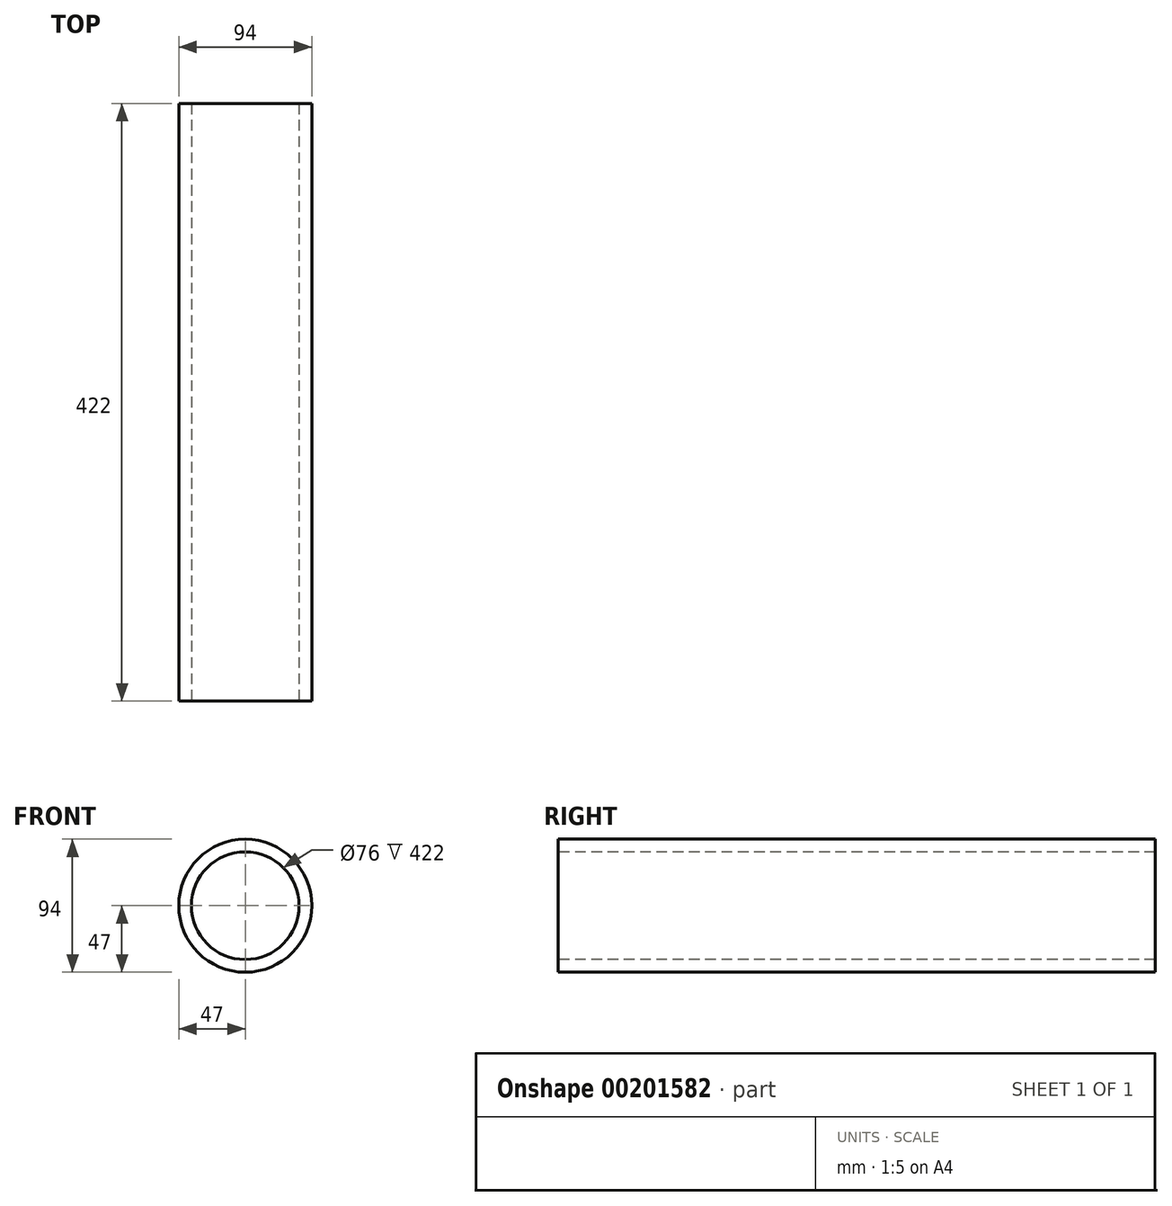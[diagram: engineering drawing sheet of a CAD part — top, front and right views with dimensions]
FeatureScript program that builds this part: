
annotation { "Feature Type Name" : "Feature", "Feature Type Description" : "" }
export const myFeature = defineFeature(function(context is Context, id is Id, definition is map)
    precondition{}
    {
        {
            var Q0;
            Q0=qCreatedBy(makeId("Front.planeOp"),FACE);
            var sketch = newSketch(context, id + "F0", { "sketchPlane" : qUnion([Q0])});
            skCircle(sketch, "E0", {"center": v(0, 0) * mm, "radius": 38 * mm});
            skCircle(sketch, "E1", {"center": v(0, 0) * mm, "radius": 47 * mm});
            skSolve(sketch);
        }
        {
            var Q0;
            Q0 = qSketchRegion(id + "F0", true);
            extrude(context, id + "F1", {"entities" : qUnion([Q0]), "oppositeDirection" : true, "depth" : 422 * mm});
        }
    });
